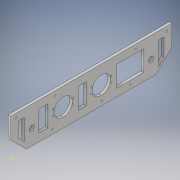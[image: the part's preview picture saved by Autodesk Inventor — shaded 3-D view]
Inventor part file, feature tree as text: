
AUTODESK INVENTOR PART (.ipt)
format: ipt  version: 2017 (Build 210142000, 142)  size: 293,888 bytes
history: native  units: in
note: dims shown in document units (in); Inventor stores cm internally (conversion verified against a paired STEP export)
features: sketch x15, hole x8, extrude x7, chamfer x2, thicken_offset x1, projected_geometry x1
ambient origin geometry x8: Origin, YZ Plane, XZ Plane, XY Plane, X Axis, Y Axis, Z Axis, Center Point
bodies: Solid1 (feature_tree)
feature tree (34):
  extrude  "Extrusion1"  Depth=15.5in
  sketch  "Sketch3"  dims[d4=2.0in]
  sketch  "Sketch4"  dims[d5=1.0in]
  chamfer  "Chamfer1"  Distance=0.25in
  chamfer  "Chamfer2"  Distance=1.5in Angle=45.0deg
  hole  "Hole1"  [1 undecoded]
  hole  "Hole3"  [1 undecoded]
  sketch  "Sketch8"  dims[d13=1.5in d14=0.125in d15=45.0deg d16=2.0in]
  hole  "Hole4"  [1 undecoded]
  hole  "Hole6"  [1 undecoded]
  extrude  "Extrusion2"  Depth=0.5in
  thicken_offset  "Thicken1"
  sketch  "Sketch16"  dims[d20=0.501in d21=0.75in d22=0.375in d23=0.25in d24=0.5635in d25=1.0in d26=0.8108in d42=0.394in]
  sketch  "Sketch17"  dims[d43=3.75in d44=3.75in]
  sketch  "Sketch18"  dims[d45=0.144in d46=0.5in]
  hole  "Hole10"  [1 undecoded]
  hole  "Hole11"  [1 undecoded]
  hole  "Hole12"  [1 undecoded]
  hole  "Hole13"  [1 undecoded]
  sketch  "Sketch19"  dims[d47=0.5in]
  sketch  "Sketch20"  dims[d48=0.188in d49=0.75in d50=0.375in d51=0.25in d52=0.5635in d53=1.0in d54=0.8108in d57=0.394in]
  extrude  "Extrusion3"  Depth=0.75in
  extrude  "Extrusion4"  Depth=0.75in
  sketch  "Sketch21"  dims[d61=0.14in d62=0.75in d63=0.375in d64=0.25in d65=0.5635in d66=1.0in d67=0.8108in]
  extrude  "Extrusion5"  Depth=0.75in
  extrude  "Extrusion6"  Depth=0.75in
  extrude  "Extrusion7"  Depth=0.75in
  sketch  "Sketch1"  dims[d2=3.25in d3=15.5in]
  sketch  "Sketch5"  dims[d6=2.0in]
  projected_geometry  "Projected Loop1"
  sketch  "Sketch7"  dims[d7=1.0in d8=0.25in d9=0.0in d10=1.5in d11=0.125in d12=45.0deg]
  sketch  "Sketch10"  dims[d17=1.5in d18=1.5in]
  sketch  "Sketch14"  dims[d19=2.0in]
  sketch  "Sketch22"  dims[d75=1.7in d76=0.75in d77=0.375in d78=0.25in d79=0.5635in d80=1.0in d81=0.8108in d82=0.144in d108=1.5in d109=1.5in d113=0.945in d114=0.276in d115=0.276in d116=0.945in d117=0.945in d118=0.945in d119=0.138in d120=0.138in d121=0.138in d122=0.138in d123=0.138in d124=1.0in d125=0.0in d128=8.75in d129=0.25in d130=0.25in d131=0.4in d132=0.4in d133=3.0in d135=0.14in d136=3.5in d138=0.14in d139=0.394in d141=4.0in d143=4.0in d145=0.188in d146=0.188in d147=0.14in d148=0.75in d149=0.375in d150=0.25in d151=0.5635in d152=1.0in d153=0.8108in d154=0.14in d155=0.75in d156=0.375in d157=0.25in d158=0.5635in d159=1.0in d160=0.8108in d161=0.14in d162=0.75in d163=0.375in d164=0.25in d165=0.5635in d166=1.0in d167=0.8108in d168=0.14in d169=0.75in d170=0.375in d171=0.25in d172=0.5635in d173=1.0in d174=0.8108in d183=0.75in d184=0.75in d185=0.75in d186=0.45in d187=0.45in d188=0.45in d189=0.45in d190=0.75in d191=1.0in d192=0.0in d193=1.0in d194=0.0in d195=0.75in d196=0.45in d197=0.45in d198=0.75in d199=0.75in d200=0.75in d201=0.45in d202=0.45in d203=1.0in d204=0.0in d205=1.0in d206=0.0in d207=0.75in d208=0.45in d209=0.75in d210=1.0in d211=0.0in d177=1.0in d178=1.0in]
note: 8 required parameter values undecoded (feature->parameter linkage not recoverable at this tier; creation-order binding heuristic only, values carry confidence <= 0.55)
